# Revit family: P5000KO_Beam
name_source: partatom
category: Structural Framing
units: mm (PartAtom-declared; Revit-internal decimal feet)

## family parameters
Always export as geometry = No
Always vertical = Yes
Cut with Voids When Loaded = No
Material for Model Behavior = Steel
OmniClass Number = 23.25.30.11.14.14
OmniClass Title = Beams
Section Shape = Not Defined
Shared = Yes
Show family pre-cut in plan views = Yes
Structural Framing Length Roundoff = 0 "

## types (4) — shared parameters
Assembly Code = B10
Description = P5000KO - Beam - 1-5/8" x 3-1/4", 12 Gauge; Knock Outs
Disclaimer = https://www.unistrut.us
Height = 3.25 "
Manufacturer = Atkore Unistrut
Model = P5000KO
Salsify ID1 = US-P5000KO
URL = https://www.atkore.com
Unit Weight = 3.05 lb/ft

## per-type parameters (varying)
| type | Power-Strut Part Number | Structural Material | UPC-10ft | UPC-20ft |
| P5000KO GR |  | Green |  | "786364040400" |
| P5000KO HG |  | Hot Dip Galvanized | "786364040370" | "786364040417" |
| P5000KO PG | PS 100 KO6 PGAL | Pre-Galvanized | "786364040387" | "786364040424" |
| P5000KO PL |  | Plain | "786364040394" | "786364040431" |

note: column(s) folded — value = type name in every type: Part Number

## geometry (parser evidence)
native form markers: Sweep x10
no freeform markers — native parametric forms only
